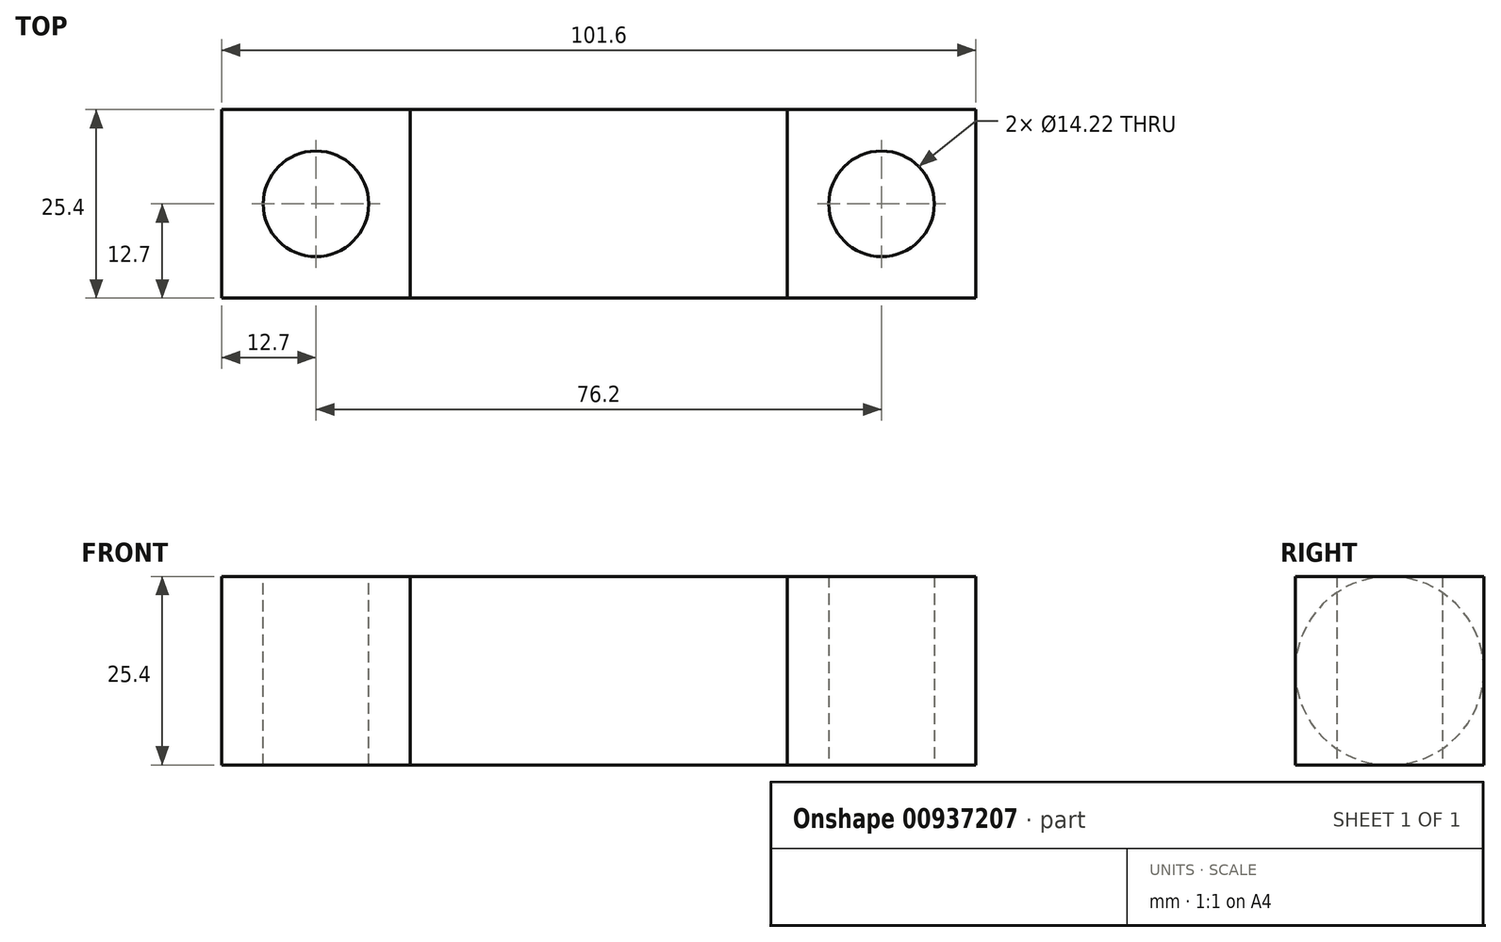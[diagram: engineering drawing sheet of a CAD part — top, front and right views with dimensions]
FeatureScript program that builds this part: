
annotation { "Feature Type Name" : "Feature", "Feature Type Description" : "" }
export const myFeature = defineFeature(function(context is Context, id is Id, definition is map)
    precondition{}
    {
        {
            var Q0;
            Q0=qCreatedBy(makeId("Top.planeOp"),FACE);
            var sketch = newSketch(context, id + "F0", { "sketchPlane" : qUnion([Q0])});
            skLineSegment(sketch, "E0.bottom", {"start": v(12.7, 12.7) * mm, "end": v(-12.7, 12.7) * mm});
            skLineSegment(sketch, "E0.top", {"start": v(12.7, -12.7) * mm, "end": v(-12.7, -12.7) * mm});
            skLineSegment(sketch, "E0.left", {"start": v(12.7, 12.7) * mm, "end": v(12.7, -12.7) * mm});
            skLineSegment(sketch, "E0.right", {"start": v(-12.7, 12.7) * mm, "end": v(-12.7, -12.7) * mm});
            skPoint(sketch, "E0.middle", {"position": v(0, 0) * mm});
            skCircle(sketch, "E1", {"center": v(0, 0) * mm, "radius": 7.11 * mm});
            skSolve(sketch);
        }
        {
            var Q0;
            Q0=makeQuery(id+"F0.imprint","IMPRINT",FACE,{"disambiguationData":[TD([[makeQuery(id+"F0.imprint","IMPRINT",EDGE,{"derivedFrom":sQuery(id+"F0.wireOp",EDGE,"E0.bottom")}),1.0]])]});
            extrude(context, id + "F1", {"entities" : qUnion([Q0]), "depth" : 25.4 * mm, "offsetDistance" : 25.4 * mm});
        }
        {
            var Q0;
            Q0=makeQuery(id+"F1.opExtrude","SWEPT_FACE",FACE,{"disambiguationData":[OSD([sQuery(id+"F0.wireOp",EDGE,"E0.right")])]});
            var sketch = newSketch(context, id + "F2", { "sketchPlane" : qUnion([Q0])});
            skLineSegment(sketch, "E2", {"start": v(0, 0) * mm, "end": v(0, 25.4) * mm, "construction": true});
            skCircle(sketch, "E3", {"center": v(0, 12.7) * mm, "radius": 12.7 * mm});
            skSolve(sketch);
        }
        {
            var Q0;
            {var subQ0=sQuery(id+"F2.wireOp",EDGE,"E3");var subQ1=sQuery(id+"F0.wireOp",EDGE,"E0.right");var subQ2=makeQuery(id+"F1.opExtrude","CAP_EDGE",EDGE,{"disambiguationData":[OSD([subQ1])],"isStart":false});var subQ3=makeQuery(id+"F2.imprint","INTERSECT",VERTEX,{"derivedFrom":[subQ2,subQ0]});Q0=makeQuery(id+"F2.imprint","IMPRINT",FACE,{"disambiguationData":[TD([[makeQuery(id+"F2.imprint","IMPRINT",EDGE,{"disambiguationData":[TD([[subQ3,-1.0]])],"derivedFrom":subQ0}),-1.0]])]});}
            var Q1;
            {var subQ0=sQuery(id+"F2.wireOp",EDGE,"E3");var subQ1=sQuery(id+"F0.wireOp",EDGE,"E0.right");var subQ2=makeQuery(id+"F1.opExtrude","CAP_EDGE",EDGE,{"disambiguationData":[OSD([subQ1])],"isStart":false});var subQ3=makeQuery(id+"F2.imprint","INTERSECT",VERTEX,{"derivedFrom":[subQ2,subQ0]});Q1=makeQuery(id+"F2.imprint","IMPRINT",FACE,{"disambiguationData":[TD([[makeQuery(id+"F2.imprint","IMPRINT",EDGE,{"disambiguationData":[TD([[subQ3,1.0]])],"derivedFrom":subQ0}),-1.0]])]});}
            var Q2;
            {var subQ0=sQuery(id+"F2.wireOp",EDGE,"E3");var subQ1=sQuery(id+"F0.wireOp",EDGE,"E0.right");var subQ4=makeQuery(id+"F1.opExtrude","CAP_EDGE",EDGE,{"disambiguationData":[OSD([subQ1])],"isStart":true});var subQ5=makeQuery(id+"F2.imprint","INTERSECT",VERTEX,{"derivedFrom":[subQ4,subQ0]});Q2=makeQuery(id+"F2.imprint","IMPRINT",FACE,{"disambiguationData":[TD([[makeQuery(id+"F2.imprint","IMPRINT",EDGE,{"disambiguationData":[TD([[subQ5,-1.0]])],"derivedFrom":subQ0}),-1.0]])]});}
            var Q3;
            {var subQ0=sQuery(id+"F2.wireOp",EDGE,"E3");var subQ1=sQuery(id+"F0.wireOp",EDGE,"E0.right");var subQ4=makeQuery(id+"F1.opExtrude","CAP_EDGE",EDGE,{"disambiguationData":[OSD([subQ1])],"isStart":true});var subQ5=makeQuery(id+"F2.imprint","INTERSECT",VERTEX,{"derivedFrom":[subQ4,subQ0]});Q3=makeQuery(id+"F2.imprint","IMPRINT",FACE,{"disambiguationData":[TD([[makeQuery(id+"F2.imprint","IMPRINT",EDGE,{"disambiguationData":[TD([[subQ5,1.0]])],"derivedFrom":subQ0}),-1.0]])]});}
            var Q4;
            {var subQ0=sQuery(id+"F2.wireOp",EDGE,"E3");var subQ1=sQuery(id+"F0.wireOp",EDGE,"E0.right");var subQ2=makeQuery(id+"F2.imprint","INTERSECT",VERTEX,{"derivedFrom":[makeQuery(id+"F1.opExtrude","CAP_EDGE",EDGE,{"disambiguationData":[OSD([subQ1])],"isStart":false}),subQ0]});Q4=makeQuery(id+"F2.imprint","IMPRINT",FACE,{"disambiguationData":[TD([[makeQuery(id+"F2.imprint","IMPRINT",EDGE,{"disambiguationData":[TD([[subQ2,1.0]])],"derivedFrom":subQ0}),1.0]])]});}
            extrude(context, id + "F3", {"entities" : qUnion([Q0, Q1, Q2, Q3, Q4]), "operationType" : NewBodyOperationType.ADD, "depth" : 76.2 * mm, "offsetDistance" : 25.4 * mm});
        }
        {
            var Q0;
            {var subQ0=sQuery(id+"F0.wireOp",EDGE,"E0.right");var subQ1=makeQuery(id+"F1.opExtrude","CAP_EDGE",EDGE,{"disambiguationData":[OSD([subQ0])],"isStart":false});var subQ2=sQuery(id+"F0.wireOp",EDGE,"E0.top");var subQ3=makeQuery(id+"F2.imprint","INTERSECT",VERTEX,{"derivedFrom":[subQ1,sQuery(id+"F2.wireOp",EDGE,"E3")]});var subQ4=sQuery(id+"F0.wireOp",EDGE,"E0.bottom");Q0=makeQuery(id+"F3.boolean.opBoolean","MERGE",FACE,{"derivedFrom":[makeQuery(id+"F1.opExtrude","CAP_FACE",FACE,{"disambiguationData":[OSD([subQ4,subQ2,sQuery(id+"F0.wireOp",EDGE,"E0.left"),subQ0,sQuery(id+"F0.wireOp",EDGE,"E1")])],"isStart":false}),makeQuery(id+"F3.opExtrude","SWEPT_FACE",FACE,{"disambiguationData":[OSD([subQ0]),TDD([makeQuery(id+"F2.imprint","IMPRINT",EDGE,{"disambiguationData":[TD([[subQ3,1.0]])],"derivedFrom":subQ1}),makeQuery(id+"F2.imprint","IMPRINT",EDGE,{"disambiguationData":[TD([[subQ3,-1.0]])],"derivedFrom":subQ1})])]})]});}
            var sketch = newSketch(context, id + "F4", { "sketchPlane" : qUnion([Q0])});
            skCircle(sketch, "E4", {"center": v(-76.2, 0) * mm, "radius": 7.11 * mm});
            skLineSegment(sketch, "E5", {"start": v(-88.9, 0) * mm, "end": v(-76.2, 0) * mm, "construction": true});
            skLineSegment(sketch, "E6", {"start": v(12.7, 0) * mm, "end": v(-12.7, 0) * mm, "construction": true});
            skLineSegment(sketch, "E7", {"start": v(-12.7, 0) * mm, "end": v(-63.5, 0) * mm, "construction": true});
            skPoint(sketch, "E8", {"position": v(-63.5, 0) * mm});
            skLineSegment(sketch, "E9", {"start": v(-63.5, 0) * mm, "end": v(-76.2, 0) * mm, "construction": true});
            skLineSegment(sketch, "E10.bottom", {"start": v(-12.7, 12.7) * mm, "end": v(-63.5, 12.7) * mm});
            skLineSegment(sketch, "E10.top", {"start": v(-12.7, -12.7) * mm, "end": v(-63.5, -12.7) * mm});
            skLineSegment(sketch, "E10.left", {"start": v(-12.7, 12.7) * mm, "end": v(-12.7, -12.7) * mm});
            skLineSegment(sketch, "E10.right", {"start": v(-63.5, 12.7) * mm, "end": v(-63.5, -12.7) * mm});
            skPoint(sketch, "E10.middle", {"position": v(-38.1, 0) * mm});
            skSolve(sketch);
        }
        {
            var Q0;
            Q0=makeQuery(id+"F4.imprint","IMPRINT",FACE,{"disambiguationData":[TD([[makeQuery(id+"F4.imprint","IMPRINT",EDGE,{"derivedFrom":sQuery(id+"F4.wireOp",EDGE,"E4")}),1.0]])]});
            var Q1;
            Q1=makeQuery(id+"F4.imprint","IMPRINT",FACE,{"disambiguationData":[TD([[makeQuery(id+"F4.imprint","IMPRINT",EDGE,{"derivedFrom":sQuery(id+"F4.wireOp",EDGE,"E10.bottom")}),1.0]])]});
            extrude(context, id + "F5", {"entities" : qUnion([Q0, Q1]), "operationType" : NewBodyOperationType.REMOVE, "endBound" : BoundingType.THROUGH_ALL, "oppositeDirection" : true, "depth" : 25.4 * mm, "offsetDistance" : 25.4 * mm});
        }
        {
            var Q0;
            {var subQ0=sQuery(id+"F2.wireOp",EDGE,"E3");var subQ1=sQuery(id+"F0.wireOp",EDGE,"E0.right");var subQ2=makeQuery(id+"F2.imprint","INTERSECT",VERTEX,{"derivedFrom":[makeQuery(id+"F1.opExtrude","CAP_EDGE",EDGE,{"disambiguationData":[OSD([subQ1])],"isStart":false}),subQ0]});Q0=makeQuery(id+"F2.imprint","IMPRINT",FACE,{"disambiguationData":[TD([[makeQuery(id+"F2.imprint","IMPRINT",EDGE,{"disambiguationData":[TD([[subQ2,1.0]])],"derivedFrom":subQ0}),1.0]])]});}
            extrude(context, id + "F6", {"entities" : qUnion([Q0]), "operationType" : NewBodyOperationType.ADD, "endBound" : BoundingType.UP_TO_NEXT, "depth" : 25.4 * mm, "offsetDistance" : 25.4 * mm});
        }
        {
            var Q0;
            {var subQ0=sQuery(id+"F0.wireOp",EDGE,"E0.right");var subQ1=sQuery(id+"F0.wireOp",EDGE,"E0.bottom");var subQ2=sQuery(id+"F0.wireOp",EDGE,"E0.top");var subQ3=makeQuery(id+"F1.opExtrude","CAP_EDGE",EDGE,{"disambiguationData":[OSD([subQ0])],"isStart":true});var subQ4=makeQuery(id+"F2.imprint","INTERSECT",VERTEX,{"derivedFrom":[subQ3,sQuery(id+"F2.wireOp",EDGE,"E3")]});Q0=makeQuery(id+"F5.boolean.opBoolean","SPLIT",FACE,{"disambiguationData":[TD([makeQuery(id+"F5.opExtrude","SWEPT_FACE",FACE,{"disambiguationData":[OSD([sQuery(id+"F4.wireOp",EDGE,"E4")])]})])],"derivedFrom":makeQuery(id+"F3.boolean.opBoolean","MERGE",FACE,{"derivedFrom":[makeQuery(id+"F1.opExtrude","CAP_FACE",FACE,{"disambiguationData":[OSD([subQ1,subQ2,sQuery(id+"F0.wireOp",EDGE,"E0.left"),subQ0,sQuery(id+"F0.wireOp",EDGE,"E1")])],"isStart":true}),makeQuery(id+"F3.opExtrude","SWEPT_FACE",FACE,{"disambiguationData":[OSD([subQ0]),TDD([makeQuery(id+"F2.imprint","IMPRINT",EDGE,{"disambiguationData":[TD([[subQ4,1.0]])],"derivedFrom":subQ3}),makeQuery(id+"F2.imprint","IMPRINT",EDGE,{"disambiguationData":[TD([[subQ4,-1.0]])],"derivedFrom":subQ3})])]})]})});}
            var sketch = newSketch(context, id + "F7", { "sketchPlane" : qUnion([Q0])});
            skCircle(sketch, "E11", {"center": v(-76.2, 0) * mm, "radius": 7.11 * mm});
            skSolve(sketch);
        }
        {
            var Q0;
            Q0=makeQuery(id+"F7.imprint","IMPRINT",FACE,{"disambiguationData":[TD([[makeQuery(id+"F7.imprint","IMPRINT",EDGE,{"derivedFrom":sQuery(id+"F7.wireOp",EDGE,"E11")}),-1.0]])]});
            var Q1;
            Q1=sQuery(id+"F7.wireOp",EDGE,"E11");
            extrude(context, id + "F8", {"entities" : qUnion([Q0]), "operationType" : NewBodyOperationType.REMOVE, "surfaceEntities" : qUnion([Q1]), "endBound" : BoundingType.THROUGH_ALL, "depth" : 25.4 * mm, "offsetDistance" : 25.4 * mm});
        }
    });
